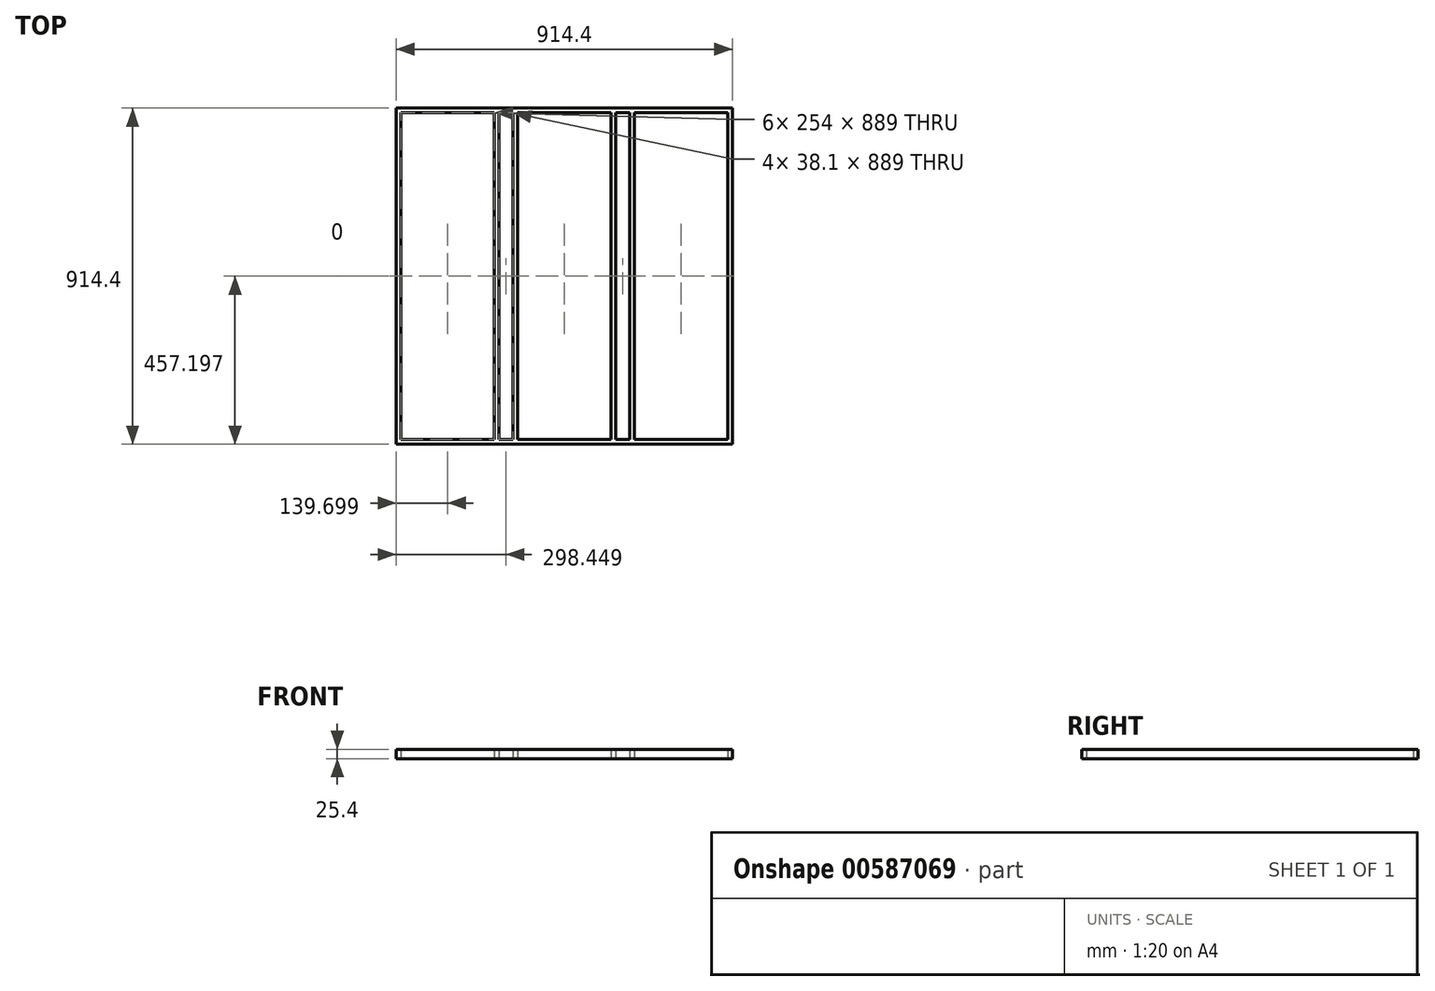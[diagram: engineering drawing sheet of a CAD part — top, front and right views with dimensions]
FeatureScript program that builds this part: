
annotation { "Feature Type Name" : "Feature", "Feature Type Description" : "" }
export const myFeature = defineFeature(function(context is Context, id is Id, definition is map)
    precondition{}
    {
        {
            var Q0;
            Q0=qCreatedBy(makeId("Top.planeOp"),FACE);
            var sketch = newSketch(context, id + "F0", { "sketchPlane" : qUnion([Q0])});
            skLineSegment(sketch, "E0", {"start": v(-422.96, 560.23) * mm, "end": v(-422.96, -354.17) * mm});
            skLineSegment(sketch, "E1", {"start": v(-422.96, -354.17) * mm, "end": v(491.44, -354.17) * mm});
            skLineSegment(sketch, "E2", {"start": v(491.44, -354.17) * mm, "end": v(491.44, 560.23) * mm});
            skLineSegment(sketch, "E3", {"start": v(491.44, 560.23) * mm, "end": v(-422.96, 560.23) * mm});
            skLineSegment(sketch, "E4.0", {"start": v(-410.26, 547.53) * mm, "end": v(-410.26, -341.47) * mm});
            skLineSegment(sketch, "E5.0", {"start": v(478.74, 547.53) * mm, "end": v(224.74, 547.53) * mm});
            skLineSegment(sketch, "E6.0", {"start": v(478.74, -341.47) * mm, "end": v(478.74, 547.53) * mm});
            skLineSegment(sketch, "E7.0", {"start": v(-410.26, -341.47) * mm, "end": v(-156.26, -341.47) * mm});
            skLineSegment(sketch, "E8", {"start": v(34.24, 560.23) * mm, "end": v(34.24, -354.17) * mm, "construction": true});
            skLineSegment(sketch, "E9", {"start": v(-422.96, 103.03) * mm, "end": v(491.44, 103.03) * mm, "construction": true});
            skLineSegment(sketch, "E10.0", {"start": v(173.94, 547.53) * mm, "end": v(173.94, -341.47) * mm});
            skLineSegment(sketch, "E11.0", {"start": v(-105.46, 547.53) * mm, "end": v(-105.46, -341.47) * mm});
            skLineSegment(sketch, "E12.0", {"start": v(-92.76, 547.53) * mm, "end": v(-92.76, -341.47) * mm});
            skLineSegment(sketch, "E13.0", {"start": v(161.24, 547.53) * mm, "end": v(161.24, -341.47) * mm});
            skLineSegment(sketch, "E14.0", {"start": v(-143.56, 547.53) * mm, "end": v(-143.56, -341.47) * mm});
            skLineSegment(sketch, "E15.0", {"start": v(-156.26, 547.53) * mm, "end": v(-156.26, -341.47) * mm});
            skLineSegment(sketch, "E16.trimOffspring", {"start": v(-156.26, 547.53) * mm, "end": v(-410.26, 547.53) * mm});
            skLineSegment(sketch, "E17.trimOffspring", {"start": v(-105.46, 547.53) * mm, "end": v(-143.56, 547.53) * mm});
            skLineSegment(sketch, "E18.trimOffspring", {"start": v(161.24, 547.53) * mm, "end": v(-92.76, 547.53) * mm});
            skLineSegment(sketch, "E19.trimOffspring", {"start": v(-143.56, -341.47) * mm, "end": v(-105.46, -341.47) * mm});
            skLineSegment(sketch, "E20.trimOffspring", {"start": v(-92.76, -341.47) * mm, "end": v(161.24, -341.47) * mm});
            skLineSegment(sketch, "E21.trimOffspring", {"start": v(173.94, -341.47) * mm, "end": v(212.04, -341.47) * mm});
            skLineSegment(sketch, "E22.0", {"start": v(212.04, -341.47) * mm, "end": v(212.04, 547.53) * mm});
            skLineSegment(sketch, "E23.0", {"start": v(224.74, -341.47) * mm, "end": v(224.74, 547.53) * mm});
            skLineSegment(sketch, "E24.trimOffspring", {"start": v(212.04, 547.53) * mm, "end": v(173.94, 547.53) * mm});
            skLineSegment(sketch, "E25.trimOffspring", {"start": v(224.74, -341.47) * mm, "end": v(478.74, -341.47) * mm});
            skSolve(sketch);
        }
        {
            var Q0;
            Q0=makeQuery(id+"F0.imprint","IMPRINT",FACE,{"disambiguationData":[TD([[makeQuery(id+"F0.imprint","IMPRINT",EDGE,{"derivedFrom":sQuery(id+"F0.wireOp",EDGE,"E0")}),1.0]])]});
            extrude(context, id + "F1", {"entities" : qUnion([Q0]), "depth" : 25.4 * mm, "offsetDistance" : 25.4 * mm});
        }
    });
